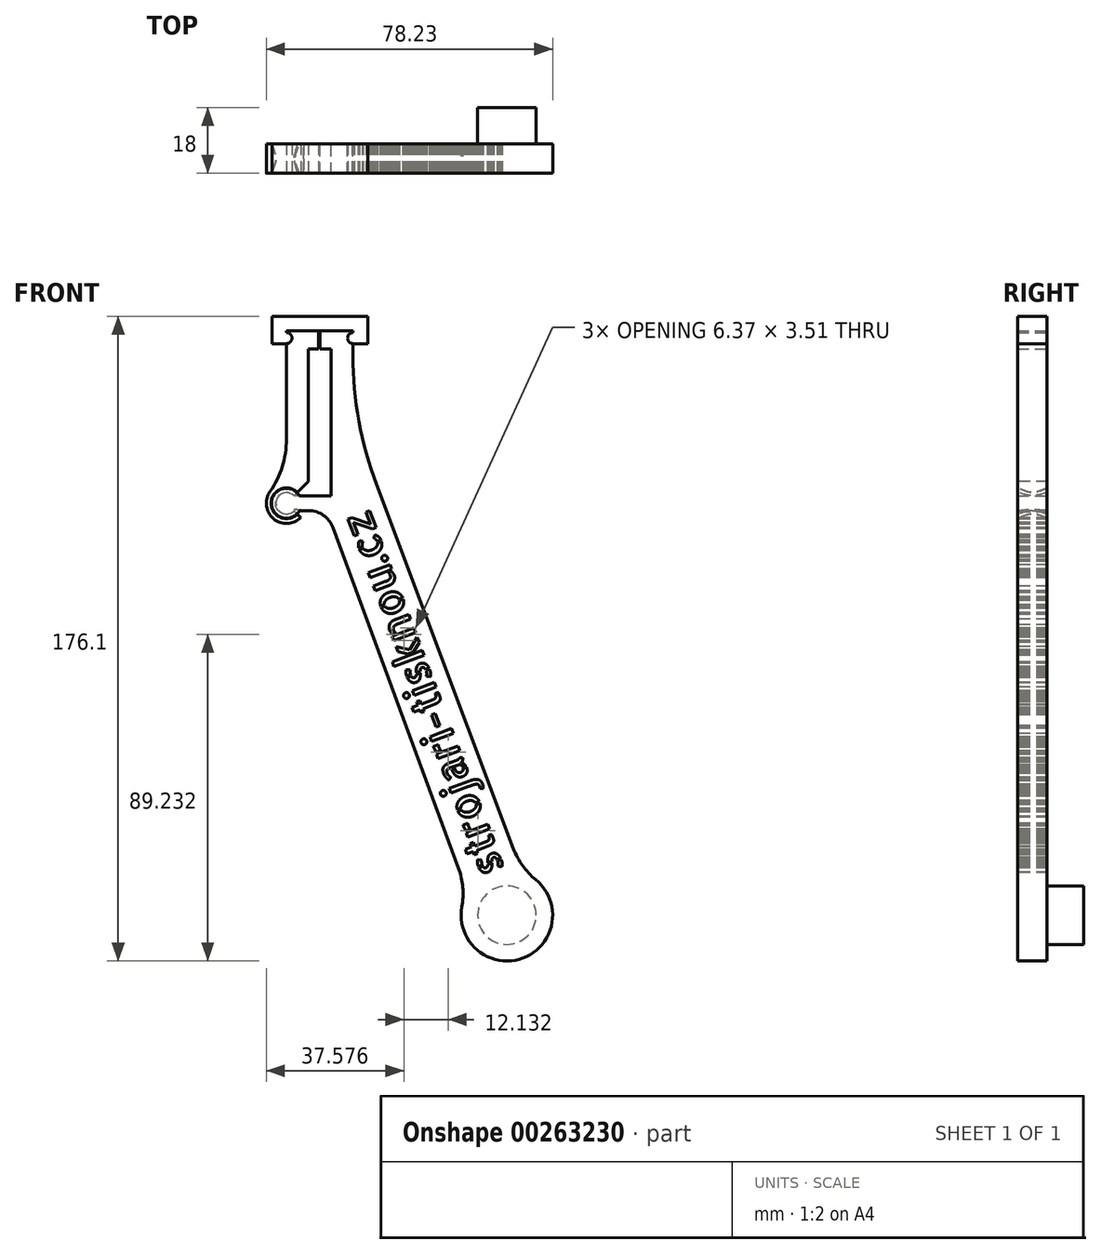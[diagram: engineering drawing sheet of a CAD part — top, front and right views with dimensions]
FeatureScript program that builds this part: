
annotation { "Feature Type Name" : "Feature", "Feature Type Description" : "" }
export const myFeature = defineFeature(function(context is Context, id is Id, definition is map)
    precondition{}
    {
        {
            var Q0;
            Q0=qCreatedBy(makeId("Front.planeOp"),FACE);
            var sketch = newSketch(context, id + "F0", { "sketchPlane" : qUnion([Q0])});
            skLineSegment(sketch, "E0.bottom", {"start": v(-6.2, -40.1) * mm, "end": v(0, -40.1) * mm});
            skLineSegment(sketch, "E0.top", {"start": v(-6.2, 0) * mm, "end": v(0, 0) * mm});
            skLineSegment(sketch, "E0.left", {"start": v(-6.2, -40.1) * mm, "end": v(-6.2, 0) * mm});
            skArc(sketch, "E1", {"start": v(-10.1, -40.1) * mm, "mid": v(-15.09, -42.36) * mm, "end": v(-9.78, -43.7) * mm});
            skLineSegment(sketch, "E2", {"start": v(-10.1, -40.1) * mm, "end": v(-6.2, -40.1) * mm});
            skLineSegment(sketch, "E3", {"start": v(-7.5, -44.1) * mm, "end": v(-6.12, -44.1) * mm});
            skLineSegment(sketch, "E4", {"start": v(-35.74, -42.1) * mm, "end": v(27.41, -42.1) * mm, "construction": true});
            skLineSegment(sketch, "E5.top", {"start": v(0, 5) * mm, "end": v(6, 5) * mm});
            skLineSegment(sketch, "E6", {"start": v(-12.2, -24.63) * mm, "end": v(-12.2, 0) * mm});
            skLineSegment(sketch, "E7", {"start": v(-6.2, -36.1) * mm, "end": v(-10.08, -39.98) * mm});
            skLineSegment(sketch, "E8", {"start": v(-8.31, -45.99) * mm, "end": v(-10.08, -44.22) * mm});
            skArc(sketch, "E9.trimOffspring", {"start": v(-16.7, -38.95) * mm, "mid": v(-15.73, -46.31) * mm, "end": v(-8.31, -45.99) * mm});
            skArc(sketch, "E10.trimOffspring", {"start": v(-10.08, -39.98) * mm, "mid": v(-15.2, -42.1) * mm, "end": v(-10.08, -44.22) * mm});
            skLineSegment(sketch, "E11.trimOffspring", {"start": v(0, -40.1) * mm, "end": v(0, 0) * mm});
            skArc(sketch, "E12", {"start": v(-16.7, -38.95) * mm, "mid": v(-13.35, -32.14) * mm, "end": v(-12.2, -24.63) * mm});
            skLineSegment(sketch, "E13", {"start": v(-12.2, -42.1) * mm, "end": v(-10.08, -39.98) * mm, "construction": true});
            skLineSegment(sketch, "E14", {"start": v(-12.2, -42.1) * mm, "end": v(-10.08, -44.22) * mm, "construction": true});
            skLineSegment(sketch, "E15.bottom", {"start": v(0, 0) * mm, "end": v(-3, 0) * mm});
            skLineSegment(sketch, "E15.top", {"start": v(0, 5) * mm, "end": v(-3, 5) * mm});
            skLineSegment(sketch, "E15.right", {"start": v(-3, 0) * mm, "end": v(-3, 5) * mm});
            skLineSegment(sketch, "E16.bottom", {"start": v(-3.5, 5) * mm, "end": v(-12.2, 5) * mm});
            skLineSegment(sketch, "E16.top", {"start": v(-3.5, 0) * mm, "end": v(-6.2, 0) * mm});
            skLineSegment(sketch, "E16.left", {"start": v(-3.5, 5) * mm, "end": v(-3.5, 0) * mm});
            skLineSegment(sketch, "E16.right", {"start": v(-12.2, 5) * mm, "end": v(-12.2, 4.5) * mm});
            skLineSegment(sketch, "E17", {"start": v(-6.2, 0) * mm, "end": v(-6.2, 0) * mm});
            skArc(sketch, "E18", {"start": v(35.73, -152.36) * mm, "mid": v(52.36, -166.33) * mm, "end": v(55.92, -144.9) * mm});
            skLineSegment(sketch, "E19", {"start": v(0.45, -48.68) * mm, "end": v(34.82, -141.85) * mm});
            skLineSegment(sketch, "E20", {"start": v(49.83, -136.44) * mm, "end": v(12.41, -37.03) * mm});
            skLineSegment(sketch, "E21", {"start": v(48.03, -154.6) * mm, "end": v(6, -40) * mm, "construction": true});
            skArc(sketch, "E22", {"start": v(49.83, -136.44) * mm, "mid": v(52.31, -141.08) * mm, "end": v(55.92, -144.9) * mm});
            skArc(sketch, "E23", {"start": v(35.73, -152.36) * mm, "mid": v(35.98, -147.05) * mm, "end": v(34.82, -141.85) * mm});
            skArc(sketch, "E24", {"start": v(6, -1.8) * mm, "mid": v(7.62, -19.7) * mm, "end": v(12.41, -37.03) * mm});
            skArc(sketch, "E25", {"start": v(0.45, -48.68) * mm, "mid": v(-2.12, -45.36) * mm, "end": v(-6.12, -44.1) * mm});
            skLineSegment(sketch, "E26.bottom", {"start": v(10, 9) * mm, "end": v(-16.2, 9) * mm});
            skLineSegment(sketch, "E26.top", {"start": v(6, 5) * mm, "end": v(-12.2, 5) * mm});
            skLineSegment(sketch, "E27.top", {"start": v(10, 1.5) * mm, "end": v(6, 1.5) * mm});
            skLineSegment(sketch, "E27.left", {"start": v(10, 9) * mm, "end": v(10, 1.5) * mm});
            skLineSegment(sketch, "E28.top", {"start": v(-16.2, 1.5) * mm, "end": v(-12.2, 1.5) * mm});
            skLineSegment(sketch, "E28.left", {"start": v(-16.2, 9) * mm, "end": v(-16.2, 1.5) * mm});
            skLineSegment(sketch, "E28.right", {"start": v(-12.2, 14.3) * mm, "end": v(-12.2, 4.5) * mm});
            skArc(sketch, "E29", {"start": v(6, 4.5) * mm, "mid": v(4.5, 3) * mm, "end": v(6, 1.5) * mm});
            skLineSegment(sketch, "E30.trimOffspring", {"start": v(6, 4.5) * mm, "end": v(6, 5) * mm});
            skLineSegment(sketch, "E31.trimOffspring", {"start": v(6, 1.5) * mm, "end": v(6, 1.5) * mm});
            skArc(sketch, "E32", {"start": v(-12.2, 1.5) * mm, "mid": v(-10.7, 3) * mm, "end": v(-12.2, 4.5) * mm});
            skLineSegment(sketch, "E33", {"start": v(6, 3) * mm, "end": v(-22.63, 3) * mm, "construction": true});
            skLineSegment(sketch, "E34.trimOffspring", {"start": v(-12.2, 1.5) * mm, "end": v(-12.2, 0) * mm});
            skLineSegment(sketch, "E35.trimOffspring", {"start": v(-12.2, 3) * mm, "end": v(-12.2, 1.5) * mm});
            skLineSegment(sketch, "E36", {"start": v(-9.78, -43.7) * mm, "end": v(-7.5, -44.1) * mm});
            skPoint(sketch, "E37.orphan", {"position": v(37.21, -148.34) * mm});
            skPoint(sketch, "E38.orphan", {"position": v(52.23, -142.83) * mm});
            skPoint(sketch, "E39.orphan", {"position": v(6, -20) * mm});
            skLineSegment(sketch, "E40.trimOffspring", {"start": v(6, -1.8) * mm, "end": v(6, 1.5) * mm});
            skPoint(sketch, "E41.orphan", {"position": v(-2.14, -44.1) * mm});
            skPoint(sketch, "E5.bottom.start.orphan", {"position": v(0, -44.1) * mm});
            skPoint(sketch, "E42.orphan", {"position": v(-10.1, -44.1) * mm});
            skLineSegment(sketch, "E43", {"start": v(-6.2, -40.1) * mm, "end": v(-6.12, -44.1) * mm});
            skLineSegment(sketch, "E44", {"start": v(-6.2, -40.1) * mm, "end": v(-7.5, -44.1) * mm});
            skSolve(sketch);
        }
        {
            var Q0;
            Q0=qCreatedBy(makeId("Front.planeOp"),FACE);
            cPlane(context, id + "F1", {"entities" : qUnion([Q0]), "cplaneType" : CPlaneType.OFFSET, "offset" : 4 * mm, "width" : 150 * mm, "height" : 150 * mm});
        }
        {
            var Q0;
            Q0=qCreatedBy(makeId("Front.planeOp"),FACE);
            cPlane(context, id + "F2", {"entities" : qUnion([Q0]), "cplaneType" : CPlaneType.OFFSET, "offset" : 4 * mm, "oppositeDirection" : true, "width" : 150 * mm, "height" : 150 * mm});
        }
        {
            var Q0;
            Q0=qCreatedBy(id+"F1.planeOp",FACE);
            var sketch = newSketch(context, id + "F3", { "sketchPlane" : qUnion([Q0])});
            skLineSegment(sketch, "E45.bottom", {"start": v(-6.2, -40.1) * mm, "end": v(0, -40.1) * mm});
            skLineSegment(sketch, "E45.top", {"start": v(-6.2, 0) * mm, "end": v(0, 0) * mm});
            skLineSegment(sketch, "E45.left", {"start": v(-6.2, -40.1) * mm, "end": v(-6.2, 0) * mm});
            skLineSegment(sketch, "E45.right", {"start": v(0, -40.1) * mm, "end": v(0, 0) * mm});
            skArc(sketch, "E46", {"start": v(-8.62, -40.1) * mm, "mid": v(-16.3, -42.1) * mm, "end": v(-8.62, -44.1) * mm});
            skLineSegment(sketch, "E47", {"start": v(-8.62, -40.1) * mm, "end": v(0, -40.1) * mm});
            skLineSegment(sketch, "E48", {"start": v(-8.62, -44.1) * mm, "end": v(-6.12, -44.1) * mm});
            skLineSegment(sketch, "E49", {"start": v(-31.13, -42.1) * mm, "end": v(32.03, -42.1) * mm, "construction": true});
            skLineSegment(sketch, "E50.top", {"start": v(0, 5) * mm, "end": v(6, 5) * mm});
            skLineSegment(sketch, "E51", {"start": v(-12.2, -24.63) * mm, "end": v(-12.2, 0) * mm});
            skLineSegment(sketch, "E52", {"start": v(-6.2, -36.1) * mm, "end": v(-9.23, -39.13) * mm});
            skLineSegment(sketch, "E53", {"start": v(-8.31, -45.99) * mm, "end": v(-9.23, -45.07) * mm});
            skArc(sketch, "E54.trimOffspring", {"start": v(-16.7, -38.95) * mm, "mid": v(-15.73, -46.31) * mm, "end": v(-8.31, -45.99) * mm});
            skArc(sketch, "E55.trimOffspring", {"start": v(-9.23, -39.13) * mm, "mid": v(-16.4, -42.1) * mm, "end": v(-9.23, -45.07) * mm});
            skArc(sketch, "E56", {"start": v(-16.7, -38.95) * mm, "mid": v(-13.35, -32.14) * mm, "end": v(-12.2, -24.63) * mm});
            skLineSegment(sketch, "E57", {"start": v(-12.2, -42.1) * mm, "end": v(-9.23, -39.13) * mm, "construction": true});
            skLineSegment(sketch, "E58", {"start": v(-12.2, -42.1) * mm, "end": v(-9.23, -45.07) * mm, "construction": true});
            skLineSegment(sketch, "E59.bottom", {"start": v(0, 0) * mm, "end": v(-3, 0) * mm});
            skLineSegment(sketch, "E59.top", {"start": v(-0.98, 5) * mm, "end": v(-3, 5) * mm});
            skLineSegment(sketch, "E59.right", {"start": v(-3, 0) * mm, "end": v(-3, 5) * mm});
            skLineSegment(sketch, "E60.bottom", {"start": v(-3.5, 5) * mm, "end": v(-12.2, 5) * mm});
            skLineSegment(sketch, "E60.top", {"start": v(-3.5, 0) * mm, "end": v(-6.2, 0) * mm});
            skLineSegment(sketch, "E60.left", {"start": v(-3.5, 5) * mm, "end": v(-3.5, 0) * mm});
            skLineSegment(sketch, "E60.right", {"start": v(-12.2, 5) * mm, "end": v(-12.2, 4.5) * mm});
            skLineSegment(sketch, "E61", {"start": v(-6.2, 0) * mm, "end": v(-6.2, 0) * mm});
            skArc(sketch, "E62", {"start": v(35.73, -152.36) * mm, "mid": v(52.36, -166.33) * mm, "end": v(55.92, -144.9) * mm});
            skLineSegment(sketch, "E63", {"start": v(0.45, -48.68) * mm, "end": v(34.82, -141.85) * mm});
            skLineSegment(sketch, "E64", {"start": v(49.83, -136.44) * mm, "end": v(12.41, -37.03) * mm});
            skLineSegment(sketch, "E65", {"start": v(48.03, -154.6) * mm, "end": v(6, -40) * mm, "construction": true});
            skArc(sketch, "E66", {"start": v(49.83, -136.44) * mm, "mid": v(52.31, -141.08) * mm, "end": v(55.92, -144.9) * mm});
            skArc(sketch, "E67", {"start": v(35.73, -152.36) * mm, "mid": v(35.98, -147.05) * mm, "end": v(34.82, -141.85) * mm});
            skArc(sketch, "E68", {"start": v(6, -1.8) * mm, "mid": v(7.62, -19.7) * mm, "end": v(12.41, -37.03) * mm});
            skArc(sketch, "E69", {"start": v(0.45, -48.68) * mm, "mid": v(-2.12, -45.36) * mm, "end": v(-6.12, -44.1) * mm});
            skLineSegment(sketch, "E70.bottom", {"start": v(10, 9) * mm, "end": v(-16.2, 9) * mm});
            skLineSegment(sketch, "E70.top", {"start": v(6, 5) * mm, "end": v(-12.2, 5) * mm});
            skLineSegment(sketch, "E71.top", {"start": v(10, 1.5) * mm, "end": v(6, 1.5) * mm});
            skLineSegment(sketch, "E71.left", {"start": v(10, 9) * mm, "end": v(10, 1.5) * mm});
            skLineSegment(sketch, "E72.top", {"start": v(-16.2, 1.5) * mm, "end": v(-12.2, 1.5) * mm});
            skLineSegment(sketch, "E72.left", {"start": v(-16.2, 9) * mm, "end": v(-16.2, 1.5) * mm});
            skLineSegment(sketch, "E72.right", {"start": v(-12.2, 35.5) * mm, "end": v(-12.2, 4.5) * mm});
            skArc(sketch, "E73", {"start": v(6, 4.5) * mm, "mid": v(4.5, 3) * mm, "end": v(6, 1.5) * mm});
            skLineSegment(sketch, "E74.trimOffspring", {"start": v(6, 4.5) * mm, "end": v(6, 5) * mm});
            skLineSegment(sketch, "E75.trimOffspring", {"start": v(6, 1.5) * mm, "end": v(6, 1.5) * mm});
            skArc(sketch, "E76", {"start": v(-12.2, 1.5) * mm, "mid": v(-10.7, 3) * mm, "end": v(-12.2, 4.5) * mm});
            skLineSegment(sketch, "E77", {"start": v(6, 3) * mm, "end": v(-23.6, 3) * mm, "construction": true});
            skLineSegment(sketch, "E78.trimOffspring", {"start": v(-12.2, 1.5) * mm, "end": v(-12.2, 0) * mm});
            skLineSegment(sketch, "E79.trimOffspring", {"start": v(-12.2, 3) * mm, "end": v(-12.2, 1.5) * mm});
            skPoint(sketch, "E80.orphan", {"position": v(6, -20) * mm});
            skLineSegment(sketch, "E81.trimOffspring", {"start": v(6, -1.8) * mm, "end": v(6, 1.5) * mm});
            skPoint(sketch, "E82.orphan", {"position": v(37.21, -148.34) * mm});
            skPoint(sketch, "E83.orphan", {"position": v(52.23, -142.83) * mm});
            skPoint(sketch, "E84.orphan", {"position": v(-3.62, -44.1) * mm});
            skLineSegment(sketch, "E85", {"start": v(-6.2, -40.1) * mm, "end": v(-6.12, -44.1) * mm});
            skSolve(sketch);
        }
        {
            var Q0;
            Q0=qCreatedBy(id+"F2.planeOp",FACE);
            var sketch = newSketch(context, id + "F4", { "sketchPlane" : qUnion([Q0])});
            skLineSegment(sketch, "E86.bottom", {"start": v(-6.2, -40.1) * mm, "end": v(0, -40.1) * mm});
            skLineSegment(sketch, "E86.top", {"start": v(-6.2, 0) * mm, "end": v(0, 0) * mm});
            skLineSegment(sketch, "E86.left", {"start": v(-6.2, -40.1) * mm, "end": v(-6.2, 0) * mm});
            skLineSegment(sketch, "E86.right", {"start": v(0, -40.1) * mm, "end": v(0, 0) * mm});
            skArc(sketch, "E87", {"start": v(-8.62, -40.1) * mm, "mid": v(-16.3, -42.1) * mm, "end": v(-8.62, -44.1) * mm});
            skLineSegment(sketch, "E88", {"start": v(-8.62, -40.1) * mm, "end": v(0, -40.1) * mm});
            skLineSegment(sketch, "E89", {"start": v(-8.62, -44.1) * mm, "end": v(-6.12, -44.1) * mm});
            skLineSegment(sketch, "E90", {"start": v(-31.12, -42.1) * mm, "end": v(32.04, -42.1) * mm, "construction": true});
            skLineSegment(sketch, "E91.top", {"start": v(0, 5) * mm, "end": v(6, 5) * mm});
            skLineSegment(sketch, "E92", {"start": v(-12.2, -24.63) * mm, "end": v(-12.2, 0) * mm});
            skLineSegment(sketch, "E93", {"start": v(-6.2, -36.1) * mm, "end": v(-9.23, -39.13) * mm});
            skLineSegment(sketch, "E94", {"start": v(-8.31, -45.99) * mm, "end": v(-9.23, -45.07) * mm});
            skArc(sketch, "E95.trimOffspring", {"start": v(-16.7, -38.95) * mm, "mid": v(-15.73, -46.31) * mm, "end": v(-8.31, -45.99) * mm});
            skArc(sketch, "E96.trimOffspring", {"start": v(-9.23, -39.13) * mm, "mid": v(-16.4, -42.1) * mm, "end": v(-9.23, -45.07) * mm});
            skArc(sketch, "E97", {"start": v(-16.7, -38.95) * mm, "mid": v(-13.35, -32.14) * mm, "end": v(-12.2, -24.63) * mm});
            skLineSegment(sketch, "E98", {"start": v(-12.2, -42.1) * mm, "end": v(-9.23, -39.13) * mm, "construction": true});
            skLineSegment(sketch, "E99", {"start": v(-12.2, -42.1) * mm, "end": v(-9.23, -45.07) * mm, "construction": true});
            skLineSegment(sketch, "E100.bottom", {"start": v(0, 0) * mm, "end": v(-3, 0) * mm});
            skLineSegment(sketch, "E100.top", {"start": v(-1.27, 5) * mm, "end": v(-3, 5) * mm});
            skLineSegment(sketch, "E100.right", {"start": v(-3, 0) * mm, "end": v(-3, 5) * mm});
            skLineSegment(sketch, "E101.bottom", {"start": v(-3.5, 5) * mm, "end": v(-12.2, 5) * mm});
            skLineSegment(sketch, "E101.top", {"start": v(-3.5, 0) * mm, "end": v(-6.2, 0) * mm});
            skLineSegment(sketch, "E101.left", {"start": v(-3.5, 5) * mm, "end": v(-3.5, 0) * mm});
            skLineSegment(sketch, "E101.right", {"start": v(-12.2, 5) * mm, "end": v(-12.2, 4.5) * mm});
            skLineSegment(sketch, "E102", {"start": v(-6.2, 0) * mm, "end": v(-6.2, 0) * mm});
            skArc(sketch, "E103", {"start": v(35.73, -152.36) * mm, "mid": v(52.36, -166.33) * mm, "end": v(55.92, -144.9) * mm});
            skLineSegment(sketch, "E104", {"start": v(0.45, -48.68) * mm, "end": v(34.82, -141.85) * mm});
            skLineSegment(sketch, "E105", {"start": v(49.83, -136.44) * mm, "end": v(12.41, -37.03) * mm});
            skLineSegment(sketch, "E106", {"start": v(48.03, -154.6) * mm, "end": v(6, -40) * mm, "construction": true});
            skArc(sketch, "E107", {"start": v(49.83, -136.44) * mm, "mid": v(52.31, -141.08) * mm, "end": v(55.92, -144.9) * mm});
            skArc(sketch, "E108", {"start": v(35.73, -152.36) * mm, "mid": v(35.98, -147.05) * mm, "end": v(34.82, -141.85) * mm});
            skArc(sketch, "E109", {"start": v(6, -1.8) * mm, "mid": v(7.62, -19.7) * mm, "end": v(12.41, -37.03) * mm});
            skArc(sketch, "E110", {"start": v(0.45, -48.68) * mm, "mid": v(-2.12, -45.36) * mm, "end": v(-6.12, -44.1) * mm});
            skLineSegment(sketch, "E111.bottom", {"start": v(10, 9) * mm, "end": v(-16.2, 9) * mm});
            skLineSegment(sketch, "E111.top", {"start": v(6, 5) * mm, "end": v(-12.2, 5) * mm});
            skLineSegment(sketch, "E112.top", {"start": v(10, 1.5) * mm, "end": v(6, 1.5) * mm});
            skLineSegment(sketch, "E112.left", {"start": v(10, 9) * mm, "end": v(10, 1.5) * mm});
            skLineSegment(sketch, "E113.top", {"start": v(-16.2, 1.5) * mm, "end": v(-12.2, 1.5) * mm});
            skLineSegment(sketch, "E113.left", {"start": v(-16.2, 9) * mm, "end": v(-16.2, 1.5) * mm});
            skLineSegment(sketch, "E113.right", {"start": v(-12.2, 4.5) * mm, "end": v(-12.2, 4.44) * mm});
            skArc(sketch, "E114", {"start": v(6, 4.5) * mm, "mid": v(4.5, 3) * mm, "end": v(6, 1.5) * mm});
            skLineSegment(sketch, "E115.trimOffspring", {"start": v(6, 4.5) * mm, "end": v(6, 5) * mm});
            skLineSegment(sketch, "E116.trimOffspring", {"start": v(6, 1.5) * mm, "end": v(6, 1.5) * mm});
            skArc(sketch, "E117", {"start": v(-12.2, 1.5) * mm, "mid": v(-10.7, 3) * mm, "end": v(-12.2, 4.5) * mm});
            skLineSegment(sketch, "E118", {"start": v(6, 3) * mm, "end": v(-23.6, 3) * mm, "construction": true});
            skLineSegment(sketch, "E119.trimOffspring", {"start": v(-12.2, 1.5) * mm, "end": v(-12.2, 0) * mm});
            skLineSegment(sketch, "E120.trimOffspring", {"start": v(-12.2, 3) * mm, "end": v(-12.2, 1.5) * mm});
            skPoint(sketch, "E121.orphan", {"position": v(37.21, -148.34) * mm});
            skPoint(sketch, "E122.orphan", {"position": v(52.23, -142.83) * mm});
            skPoint(sketch, "E123.orphan", {"position": v(6, -20) * mm});
            skLineSegment(sketch, "E124.trimOffspring", {"start": v(6, -1.8) * mm, "end": v(6, 1.5) * mm});
            skPoint(sketch, "E125.orphan", {"position": v(-3.62, -44.1) * mm});
            skLineSegment(sketch, "E126", {"start": v(-6.12, -44.1) * mm, "end": v(-6.2, -40.1) * mm});
            skSolve(sketch);
        }
        {
            var Q0;
            Q0=makeQuery(id+"F4.imprint","IMPRINT",FACE,{"disambiguationData":[TD([[makeQuery(id+"F4.imprint","IMPRINT",EDGE,{"derivedFrom":sQuery(id+"F4.wireOp",EDGE,"E92")}),-1.0]])]});
            var Q1;
            Q1=makeQuery(id+"F0.imprint","IMPRINT",FACE,{"disambiguationData":[TD([[makeQuery(id+"F0.imprint","IMPRINT",EDGE,{"derivedFrom":sQuery(id+"F0.wireOp",EDGE,"E6")}),-1.0]])]});
            var Q2;
            Q2=makeQuery(id+"F3.imprint","IMPRINT",FACE,{"disambiguationData":[TD([[makeQuery(id+"F3.imprint","IMPRINT",EDGE,{"derivedFrom":sQuery(id+"F3.wireOp",EDGE,"E51")}),-1.0]])]});
            loft(context, id + "F5", {"sheetProfilesArray" : [{ "sheetProfileEntities" : qUnion([Q0]) }, { "sheetProfileEntities" : qUnion([Q1]) }, { "sheetProfileEntities" : qUnion([Q2]) }]});
        }
        {
            var Q0;
            Q0=qCreatedBy(id+"F1.planeOp",FACE);
            var sketch = newSketch(context, id + "F6", { "sketchPlane" : qUnion([Q0])});
            skText(sketch, "E127", { "text": "strojari-tisknou.cz", "fontName": "AllertaStencil-Regular.ttf"});
            skLineSegment(sketch, "E128.right", {"start": v(-16.74, 83.24) * mm, "end": v(-16.74, 11.03) * mm});
            skCircle(sketch, "E129", {"center": v(48.03, -154.6) * mm, "radius": 8 * mm});
            const initialGuessF6  = {"E127": [0.04739, -0.14202, -0.35228, 0.9359, 0.0083]};
            skSetInitialGuess(sketch, initialGuessF6);
            skSolve(sketch);
        }
        {
            var Q0;
            {var subQ0=sQuery(id+"F3.wireOp",EDGE,"E46");Q0=makeQuery(id+"F3.imprint","IMPRINT",FACE,{"disambiguationData":[TD([[makeQuery(id+"F3.imprint","IMPRINT",EDGE,{"derivedFrom":subQ0}),1.0]])]});}
            var Q1;
            Q1=makeQuery(id+"F0.imprint","IMPRINT",FACE,{"disambiguationData":[TD([[makeQuery(id+"F0.imprint","IMPRINT",EDGE,{"derivedFrom":sQuery(id+"F0.wireOp",EDGE,"E1")}),1.0]])]});
            var Q2;
            {var subQ0=sQuery(id+"F4.wireOp",EDGE,"E87");Q2=makeQuery(id+"F4.imprint","IMPRINT",FACE,{"disambiguationData":[TD([[makeQuery(id+"F4.imprint","IMPRINT",EDGE,{"derivedFrom":subQ0}),1.0]])]});}
            loft(context, id + "F7", {"sheetProfilesArray" : [{ "sheetProfileEntities" : qUnion([Q0]) }, { "sheetProfileEntities" : qUnion([Q1]) }, { "sheetProfileEntities" : qUnion([Q2]) }]});
        }
        {
            var Q0;
            Q0=makeQuery(id+"F0.imprint","IMPRINT",FACE,{"disambiguationData":[TD([[makeQuery(id+"F0.imprint","IMPRINT",EDGE,{"derivedFrom":sQuery(id+"F0.wireOp",EDGE,"E3")}),1.0]])]});
            extrude(context, id + "F8", {"entities" : qUnion([Q0]), "operationType" : NewBodyOperationType.ADD, "endBound" : BoundingType.SYMMETRIC, "depth" : 8 * mm});
        }
        {
            var Q0;
            Q0=makeQuery(id+"F0.imprint","IMPRINT",FACE,{"disambiguationData":[TD([[makeQuery(id+"F0.imprint","IMPRINT",EDGE,{"derivedFrom":sQuery(id+"F0.wireOp",EDGE,"E0.bottom")}),-1.0]])]});
            extrude(context, id + "F9", {"entities" : qUnion([Q0]), "operationType" : NewBodyOperationType.ADD, "endBound" : BoundingType.SYMMETRIC, "depth" : 8 * mm});
        }
        {
            var Q0;
            Q0=makeQuery(id+"F0.imprint","IMPRINT",FACE,{"disambiguationData":[TD([[makeQuery(id+"F0.imprint","IMPRINT",EDGE,{"derivedFrom":sQuery(id+"F0.wireOp",EDGE,"E27.top")}),-1.0]])]});
            var Q1;
            Q1=makeQuery(id+"F0.imprint","IMPRINT",FACE,{"disambiguationData":[TD([[makeQuery(id+"F0.imprint","IMPRINT",EDGE,{"derivedFrom":sQuery(id+"F0.wireOp",EDGE,"E28.top")}),1.0]])]});
            extrude(context, id + "F10", {"entities" : qUnion([Q0, Q1]), "endBound" : BoundingType.SYMMETRIC, "depth" : 8 * mm});
        }
        {
            var Q0;
            Q0 = qSketchRegion(id + "F6", true);
            extrude(context, id + "F11", {"entities" : qUnion([Q0]), "operationType" : NewBodyOperationType.REMOVE, "endBound" : BoundingType.THROUGH_ALL, "oppositeDirection" : true, "depth" : 25 * mm});
        }
        {
            var Q0;
            Q0=makeQuery(id+"F6.imprint","IMPRINT",FACE,{"disambiguationData":[TD([[makeQuery(id+"F6.imprint","IMPRINT",EDGE,{"derivedFrom":sQuery(id+"F6.wireOp",EDGE,"E129")}),1.0]])]});
            extrude(context, id + "F12", {"entities" : qUnion([Q0]), "operationType" : NewBodyOperationType.ADD, "oppositeDirection" : true, "depth" : 18 * mm});
        }
    });
